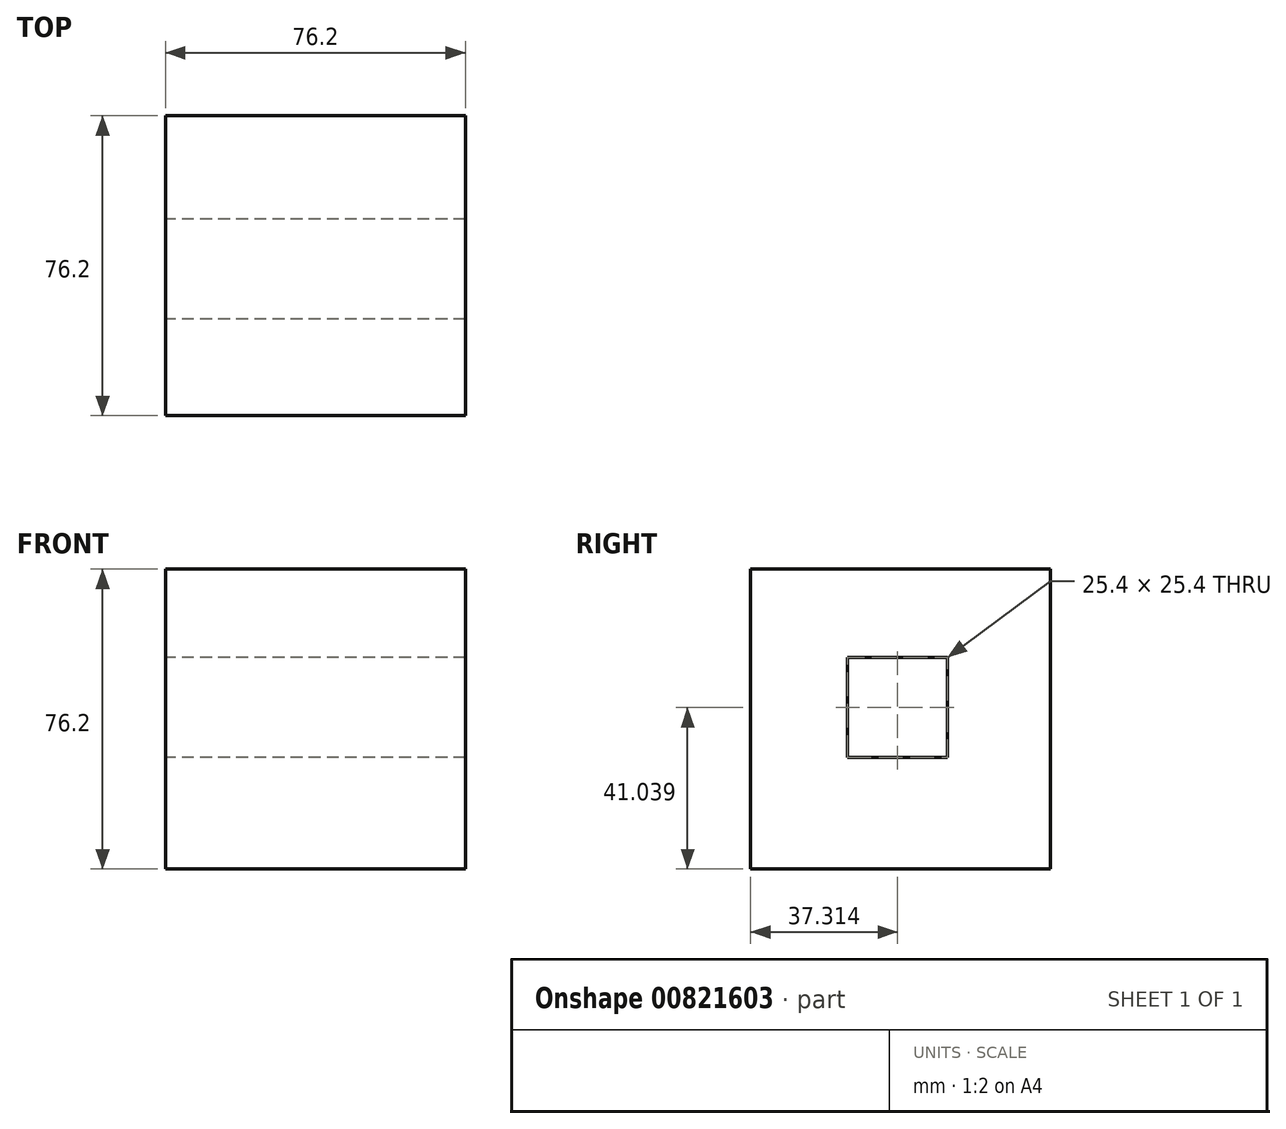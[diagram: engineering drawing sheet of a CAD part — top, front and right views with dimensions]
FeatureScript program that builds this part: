
annotation { "Feature Type Name" : "Feature", "Feature Type Description" : "" }
export const myFeature = defineFeature(function(context is Context, id is Id, definition is map)
    precondition{}
    {
        {
            var Q0;
            Q0=qCreatedBy(makeId("Front.planeOp"),FACE);
            var sketch = newSketch(context, id + "F0", { "sketchPlane" : qUnion([Q0])});
            skLineSegment(sketch, "E0.bottom", {"start": v(-40.2, 41.08) * mm, "end": v(36, 41.08) * mm});
            skLineSegment(sketch, "E0.top", {"start": v(-40.2, -35.12) * mm, "end": v(36, -35.12) * mm});
            skLineSegment(sketch, "E0.left", {"start": v(-40.2, 41.08) * mm, "end": v(-40.2, -35.12) * mm});
            skLineSegment(sketch, "E0.right", {"start": v(36, 41.08) * mm, "end": v(36, -35.12) * mm});
            skSolve(sketch);
        }
        {
            var Q0;
            Q0=makeQuery(id+"F0.imprint","IMPRINT",FACE,{"disambiguationData":[TD([[makeQuery(id+"F0.imprint","IMPRINT",EDGE,{"derivedFrom":sQuery(id+"F0.wireOp",EDGE,"E0.bottom")}),-1.0]])]});
            extrude(context, id + "F1", {"entities" : qUnion([Q0]), "depth" : 76.2 * mm, "offsetDistance" : 25.4 * mm});
        }
        {
            var Q0;
            Q0=makeQuery(id+"F1.opExtrude","SWEPT_FACE",FACE,{"disambiguationData":[OSD([sQuery(id+"F0.wireOp",EDGE,"E0.left")])]});
            var sketch = newSketch(context, id + "F2", { "sketchPlane" : qUnion([Q0])});
            skLineSegment(sketch, "E1", {"start": v(26.19, 18.62) * mm, "end": v(26.19, -6.78) * mm});
            skLineSegment(sketch, "E2", {"start": v(26.19, 18.62) * mm, "end": v(51.59, 18.62) * mm});
            skLineSegment(sketch, "E3", {"start": v(26.19, -6.78) * mm, "end": v(51.59, -6.78) * mm});
            skLineSegment(sketch, "E4", {"start": v(51.59, 18.62) * mm, "end": v(51.59, -6.78) * mm});
            skSolve(sketch);
        }
        {
            var Q0;
            Q0=makeQuery(id+"F2.imprint","IMPRINT",FACE,{"disambiguationData":[TD([[makeQuery(id+"F2.imprint","IMPRINT",EDGE,{"derivedFrom":sQuery(id+"F2.wireOp",EDGE,"E1")}),1.0]])]});
            extrude(context, id + "F3", {"entities" : qUnion([Q0]), "operationType" : NewBodyOperationType.REMOVE, "oppositeDirection" : true, "depth" : 76.2 * mm, "offsetDistance" : 25.4 * mm});
        }
    });
